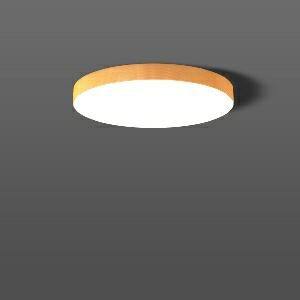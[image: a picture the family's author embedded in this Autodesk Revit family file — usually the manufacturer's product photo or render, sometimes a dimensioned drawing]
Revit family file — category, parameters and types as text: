
# Revit family: flatliner_slim_312281_002_1_5f1d
name_source: partatom
category: Lighting Fixtures
units: mm (PartAtom-declared; Revit-internal decimal feet)

## family parameters
Cut with Voids When Loaded = No
Host = Face
Light Source = No
Part Type = Normal
Room Calculation Point = No
Round Connector Dimension = Use Diameter
Shared = No

## types (1)
- 982556.002 (1 x LED Modul 840, 1700 lm, 4000)
    Apparent Load = 19 VA
    CIE Flux Codes = 45 76 94 95 100
    Color Rendering = 80
    Color Temperature = 4000
    Default Elevation = 1800 mm
    Description = Series: FLATLINER SLIM
Decorative ceiling luminaire for interior decoration. Base luminaire prepared for the installation of fabric lampshade. Base: metal, white, powder-coated. Modular design: with the basic luminaire, a cylindrical fabric lampshade with a polycarbonate satin-finish diffuser must always be ordered separately. Fabric lampshade and diffuser can be assembled without the use of tools. 
Colour: white
Diameter: 317 mm
Height: 34 mm
Lamp: LED exchangeable
Socket: without socket
Colour temperature: 4000K
Colour rendering index (CRI): 83
System power: 19 W
Rated luminous flux: 1700 lm
Beam angle Down: 117°
Luminous efficiency: 89 lm/W
Control gear: AC Strom, dim.Ph.an-/abschnitt
Protection class: I
Type of protection: IP 20
    Height = 34 mm  [stored 0.111549 ft]
    Lamp = 1 x LED Modul 840
    Lamp Light Flux = 1700 lm
    Lamp count = 1
    Length = 317 mm
    Lifetime = 50000 h
    Luminous efficacy = 89 lm/W
    Manufacturer = RZB
    ModVariant = No
    Model = 312281.002.1
    Mounting Place = Ceiling
    Mounting Type = Surface mounted
    Number of Poles = 1
    OnlyDefault = Yes
    Power Factor = 1
    Product Name = FLATLINER SLIM
    Product group = Surface mounted ceiling Fabric lampshade luminaires
    ProductGroupID = 313
    Protection Class = Protection class I
    Protection Degree = IP 20
    RLX_Detail_Level = 1
    RLX_Emergency_Light_Flux = 0 lm
    RLX_Emergency_Type = 0
    RLX_Emergency_Type_DB = No
    RlxData = <blob elided: 25145 chars, md5=a62b1321>
    Socket = socket
    Standby Power = 0 W
    System Light Flux = 1700 lm
    System Power = 19 W
    Type Image = 312287.002_982442.0063_982444.002.jpg
    URL = http://relux.com
    VarID = 982556_002_eb81
    Voltage = 230 V
    Voltage Range = 220-240 V
    Weight = 0.00 kg
    Width = 0 mm  [stored 0 ft]

note: [stored X ft] marks values corroborated as IEEE doubles in the binary element streams (Revit-internal decimal feet)

## geometry (parser evidence)
native form markers: Blend x4, Sweep x12
no freeform markers — native parametric forms only
